# Revit family: FOR UPDATE_36120XXX_NEW
name_source: partatom
category: Plumbing Fixtures
revit_build: Autodesk Revit 2018 (Build: 20170223_1515(x64)
units: mm (PartAtom-declared; Revit-internal decimal feet)

## family parameters
Always vertical = No
Cut with Voids When Loaded = No
OmniClass Number = 23.31.11.00
OmniClass Title = Faucets
Part Type = Normal
Room Calculation Point = No
Round Connector Dimension = Use Diameter
Shared = No
Work Plane-Based = Yes

## types (1)
- Default - please load Revit Family Type Catalog
    Always visible = Yes
    BIMobject category = Taps & Mixers
    Connector Description = Water Inlet 9.5mm
    Default Elevation = 1219.2 mm  [stored 4 ft]
    Description = AXOR Citterio E Single lever bidet mixer with pin handle and pop-up waste set
    Design country = Germany
    Diameter = 9.5 mm  [stored 0.031168 ft]
    EAN code = 4059625426968
    Edition number = 1
    GTIN code = https://4059625426968
    IFC Classification = Valve
    Manufacturer = AXOR
    Manufacturer country = Germany
    Manufacturer name = AXOR
    Material 1 = AXOR - Metal - 000 Chrome
    Model = 36120XXX
    OmniClass Code = 23-31 11 00
    OmniClass Description = Faucets
    Product Guid = 352240c3-fa05-4ec6-b5df-bf63e6fe7844
    Product SKU = 36120XXX
    Product data url = https://bimobject.com
    Product family = AXOR Citterio E
    Product group = Bidet mixers
    Product name = 36120XXX AXOR Citterio E Single lever bidet mixer with pin handle and pop-up waste set
    QR code = https://bimobject.com
    URL = https://www.axor-design.com
    Weight Net (Kg) = 1.8

note: [stored X ft] marks values corroborated as IEEE doubles in the binary element streams (Revit-internal decimal feet)

## geometry (parser evidence)
native form markers: Sweep x2
no freeform markers — native parametric forms only
